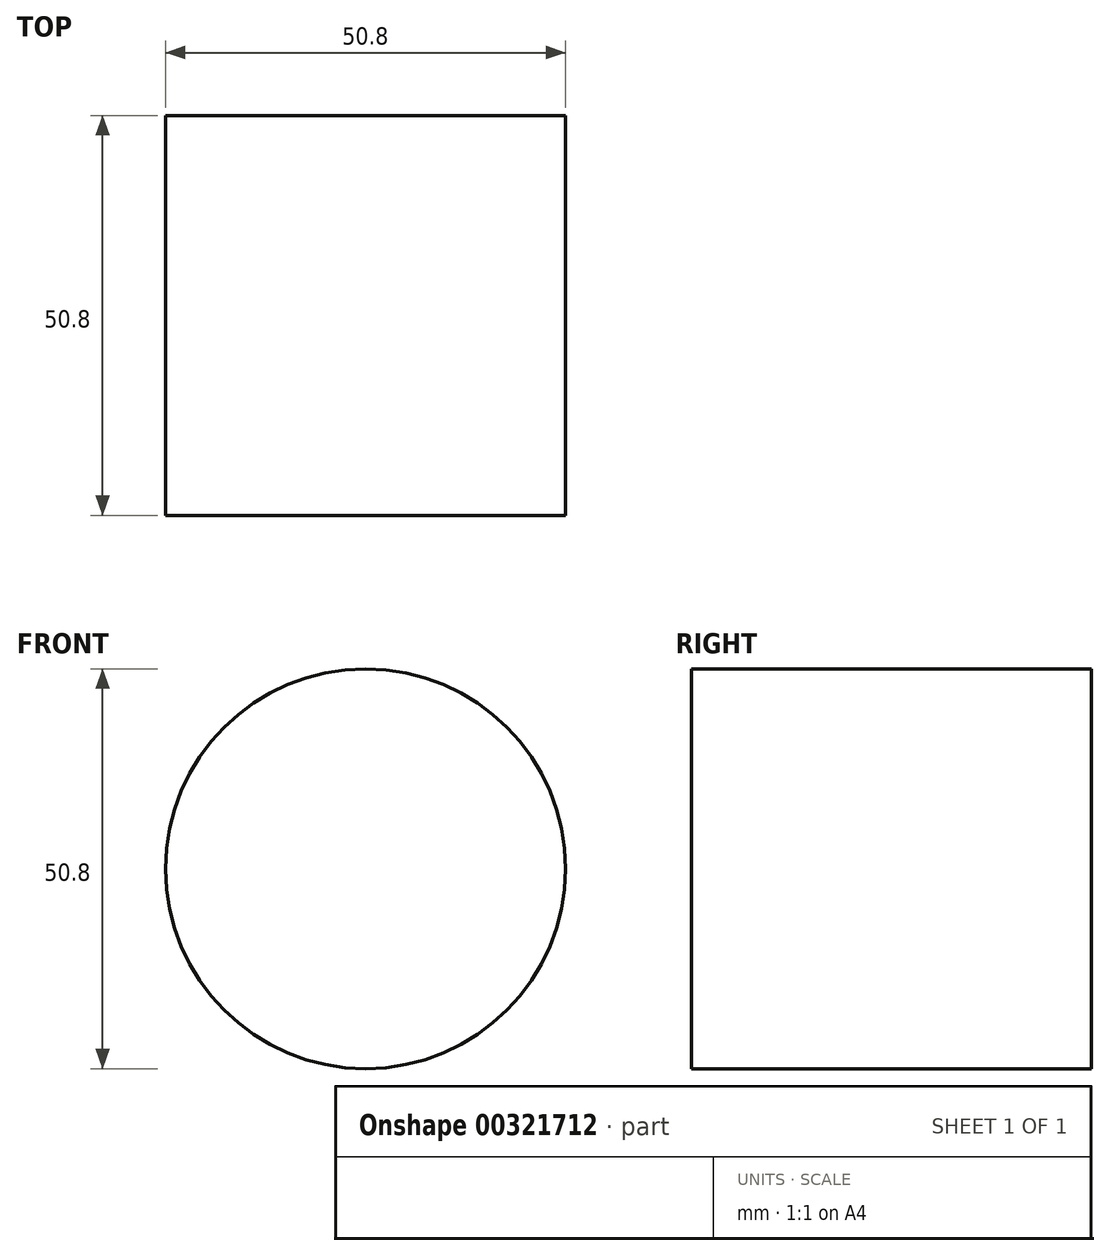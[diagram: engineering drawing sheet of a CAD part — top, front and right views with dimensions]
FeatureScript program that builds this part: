
annotation { "Feature Type Name" : "Feature", "Feature Type Description" : "" }
export const myFeature = defineFeature(function(context is Context, id is Id, definition is map)
    precondition{}
    {
        {
            var Q0;
            Q0=qCreatedBy(makeId("Front.planeOp"),FACE);
            var sketch = newSketch(context, id + "F0", { "sketchPlane" : qUnion([Q0])});
            skCircle(sketch, "E0", {"center": v(0, 0) * mm, "radius": 25.4 * mm});
            skSolve(sketch);
        }
        {
            var Q0;
            Q0=makeQuery(id+"F0.imprint","IMPRINT",FACE,{"disambiguationData":[TD([[makeQuery(id+"F0.imprint","IMPRINT",EDGE,{"derivedFrom":sQuery(id+"F0.wireOp",EDGE,"E0")}),1.0]])]});
            var sketch = newSketch(context, id + "F1", { "sketchPlane" : qUnion([Q0])});
            skSolve(sketch);
        }
        {
            var Q0;
            Q0 = qSketchRegion(id + "F1", true);
            var Q1;
            Q1=makeQuery(id+"F0.imprint","IMPRINT",FACE,{"disambiguationData":[TD([[makeQuery(id+"F0.imprint","IMPRINT",EDGE,{"derivedFrom":sQuery(id+"F0.wireOp",EDGE,"E0")}),1.0]])]});
            var Q2;
            Q2=makeQuery(id+"F1.imprint","IMPRINT",FACE,{"disambiguationData":[TD([[makeQuery(id+"F1.imprint","IMPRINT",EDGE,{"derivedFrom":makeQuery(id+"F0.imprint","IMPRINT",EDGE,{"derivedFrom":sQuery(id+"F0.wireOp",EDGE,"E0")})}),1.0]])]});
            extrude(context, id + "F2", {"entities" : qUnion([Q0, Q1, Q2]), "endBound" : BoundingType.SYMMETRIC, "depth" : 50.8 * mm});
        }
        {
            var Q0;
            Q0=qCreatedBy(makeId("Front.planeOp"),FACE);
            var Q1;
            Q1=qCreatedBy(makeId("Right.planeOp"),FACE);
            cPlane(context, id + "F3", {"entities" : qUnion([Q0, Q1]), "cplaneType" : CPlaneType.MID_PLANE, "offset" : 25.4 * mm, "width" : 152.4 * mm, "height" : 152.4 * mm});
        }
    });
